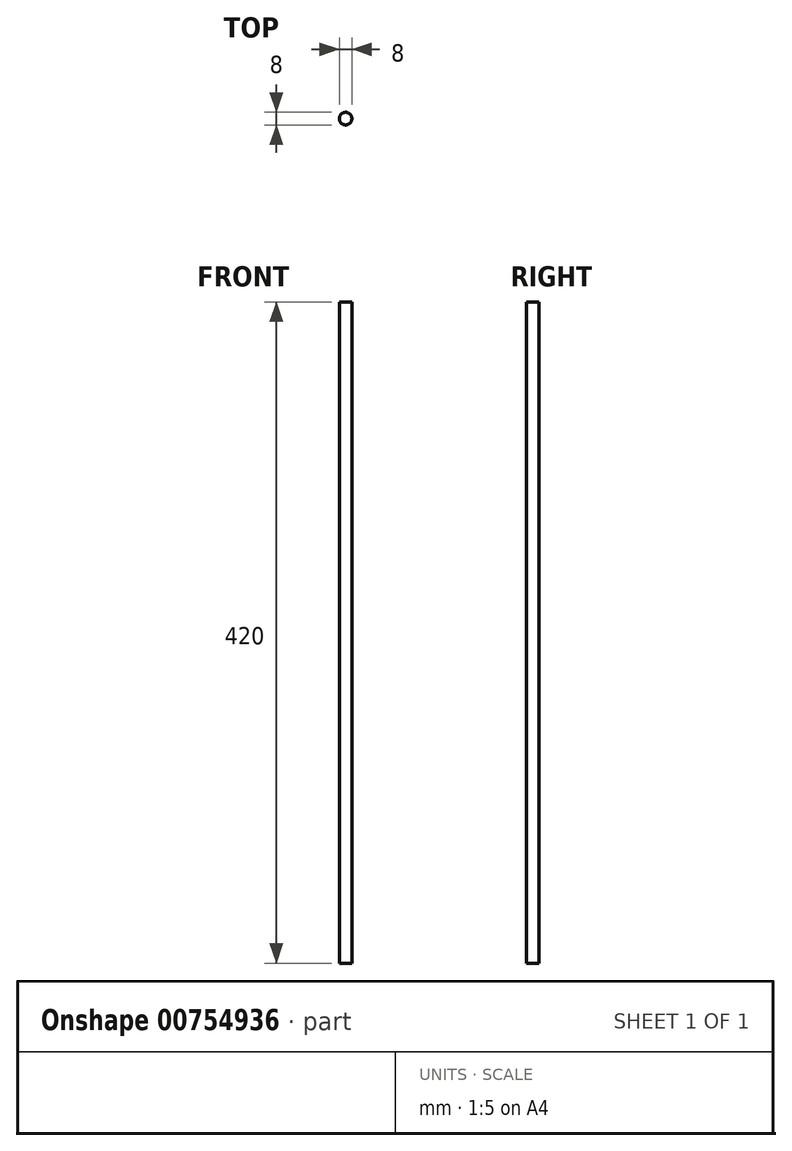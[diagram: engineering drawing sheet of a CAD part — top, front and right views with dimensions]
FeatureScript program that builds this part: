
annotation { "Feature Type Name" : "Feature", "Feature Type Description" : "" }
export const myFeature = defineFeature(function(context is Context, id is Id, definition is map)
    precondition{}
    {
        {
            var Q0;
            Q0=qCreatedBy(makeId("Top.planeOp"),FACE);
            var sketch = newSketch(context, id + "F0", { "sketchPlane" : qUnion([Q0])});
            skCircle(sketch, "E0", {"center": v(0, 0) * mm, "radius": 4 * mm});
            skSolve(sketch);
        }
        {
            var Q0;
            Q0=makeQuery(id+"F0.imprint","IMPRINT",FACE,{"disambiguationData":[TD([[makeQuery(id+"F0.imprint","IMPRINT",EDGE,{"derivedFrom":sQuery(id+"F0.wireOp",EDGE,"E0")}),1.0]])]});
            extrude(context, id + "F1", {"entities" : qUnion([Q0]), "depth" : 420 * mm, "offsetDistance" : 25 * mm});
        }
    });
